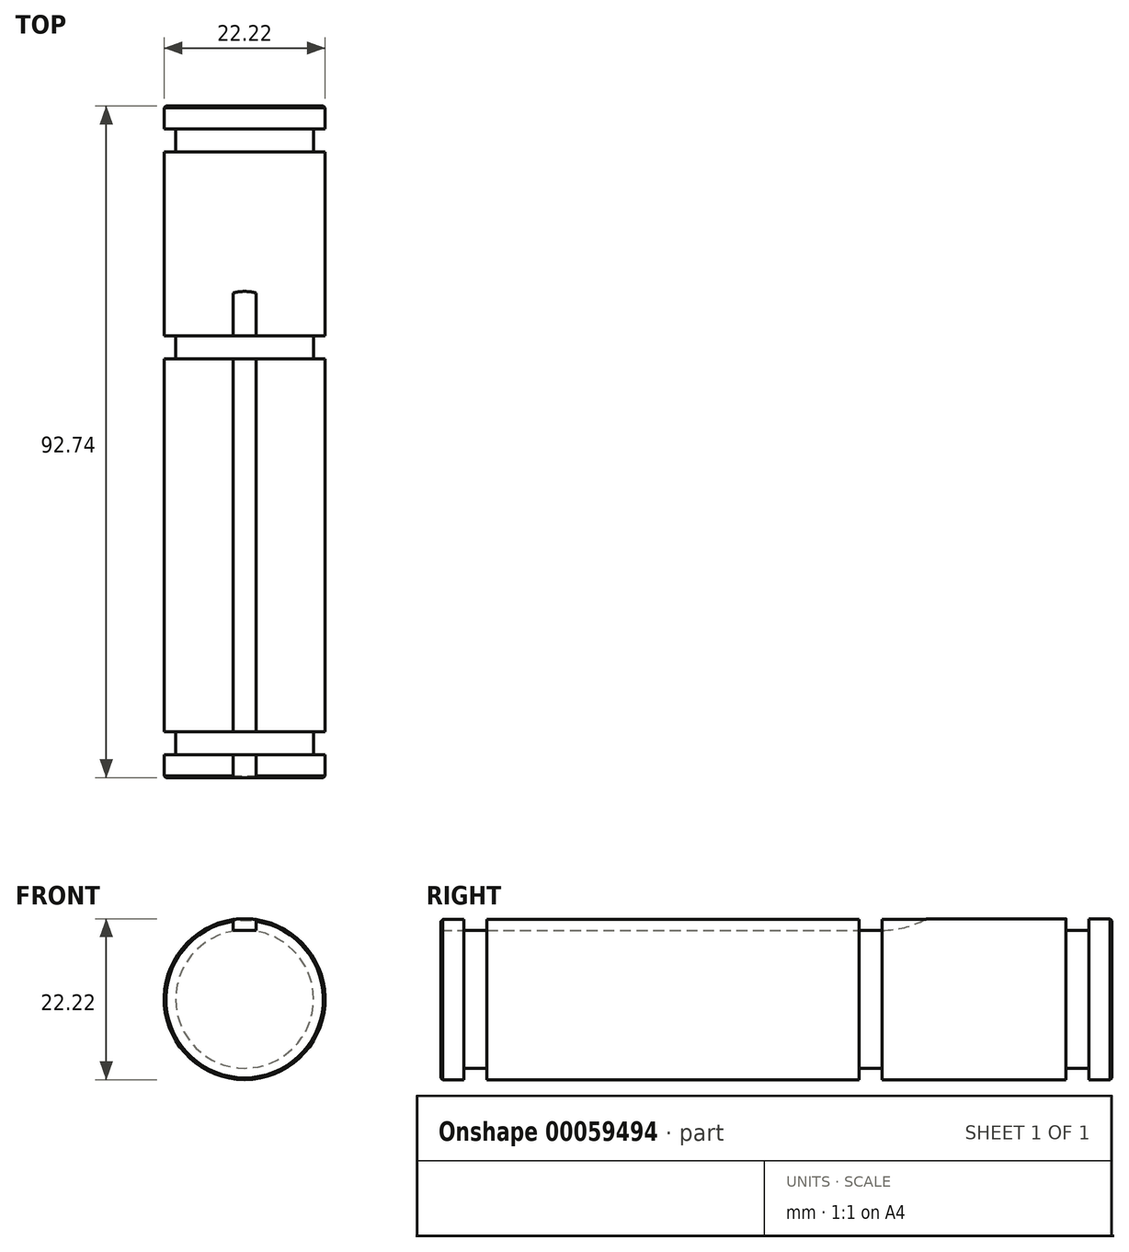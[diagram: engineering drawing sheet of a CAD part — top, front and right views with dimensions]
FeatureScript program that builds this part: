
annotation { "Feature Type Name" : "Feature", "Feature Type Description" : "" }
export const myFeature = defineFeature(function(context is Context, id is Id, definition is map)
    precondition{}
    {
        {
            var Q0;
            Q0=qCreatedBy(makeId("Front.planeOp"),FACE);
            var sketch = newSketch(context, id + "F0", { "sketchPlane" : qUnion([Q0])});
            skCircle(sketch, "E0", {"center": v(0, 0) * mm, "radius": 11.11 * mm});
            skSolve(sketch);
        }
        {
            var Q0;
            Q0=makeQuery(id+"F0.imprint","IMPRINT",FACE,{"disambiguationData":[TD([[makeQuery(id+"F0.imprint","IMPRINT",EDGE,{"derivedFrom":sQuery(id+"F0.wireOp",EDGE,"E0")}),1.0]])]});
            extrude(context, id + "F1", {"entities" : qUnion([Q0]), "oppositeDirection" : true, "depth" : 92.74 * mm});
        }
        {
            var Q0;
            Q0=qCreatedBy(makeId("Right.planeOp"),FACE);
            var sketch = newSketch(context, id + "F2", { "sketchPlane" : qUnion([Q0])});
            skLineSegment(sketch, "E1.bottom", {"start": v(0, 9.53) * mm, "end": v(60.99, 9.53) * mm});
            skLineSegment(sketch, "E1.top", {"start": v(0, 11.11) * mm, "end": v(67.13, 11.11) * mm});
            skLineSegment(sketch, "E1.left", {"start": v(0, 9.53) * mm, "end": v(0, 11.11) * mm});
            skArc(sketch, "E2.filletArc", {"start": v(60.99, 9.53) * mm, "mid": v(64.16, 9.93) * mm, "end": v(67.13, 11.11) * mm});
            skSolve(sketch);
        }
        {
            var Q0;
            Q0 = qSketchRegion(id + "F2", true);
            extrude(context, id + "F3", {"entities" : qUnion([Q0]), "operationType" : NewBodyOperationType.REMOVE, "oppositeDirection" : true, "depth" : 3.17 * mm, "symmetric" : true});
        }
        {
            var Q0;
            Q0=qCreatedBy(makeId("Right.planeOp"),FACE);
            var sketch = newSketch(context, id + "F4", { "sketchPlane" : qUnion([Q0])});
            skLineSegment(sketch, "E3.bottom", {"start": v(3.17, 9.53) * mm, "end": v(6.35, 9.53) * mm});
            skLineSegment(sketch, "E3.top", {"start": v(3.17, 11.11) * mm, "end": v(6.35, 11.11) * mm});
            skLineSegment(sketch, "E3.left", {"start": v(3.17, 9.53) * mm, "end": v(3.17, 11.11) * mm});
            skLineSegment(sketch, "E3.right", {"start": v(6.35, 9.53) * mm, "end": v(6.35, 11.11) * mm});
            skLineSegment(sketch, "E4.bottom", {"start": v(57.81, 9.53) * mm, "end": v(60.99, 9.53) * mm});
            skLineSegment(sketch, "E4.top", {"start": v(57.81, 11.11) * mm, "end": v(60.99, 11.11) * mm});
            skLineSegment(sketch, "E4.left", {"start": v(57.81, 9.53) * mm, "end": v(57.81, 11.11) * mm});
            skLineSegment(sketch, "E4.right", {"start": v(60.99, 9.53) * mm, "end": v(60.99, 11.11) * mm});
            skLineSegment(sketch, "E5.bottom", {"start": v(86.39, 9.53) * mm, "end": v(89.56, 9.53) * mm});
            skLineSegment(sketch, "E5.top", {"start": v(86.39, 11.11) * mm, "end": v(89.56, 11.11) * mm});
            skLineSegment(sketch, "E5.left", {"start": v(86.39, 9.53) * mm, "end": v(86.39, 11.11) * mm});
            skLineSegment(sketch, "E5.right", {"start": v(89.56, 9.53) * mm, "end": v(89.56, 11.11) * mm});
            skLineSegment(sketch, "E6", {"start": v(0, 0) * mm, "end": v(92.74, 0) * mm, "construction": true});
            skSolve(sketch);
        }
        {
            var Q0;
            Q0 = qSketchRegion(id + "F4", true);
            var Q1;
            Q1=sQuery(id+"F4.wireOp",EDGE,"E6");
            revolve(context, id + "F5", {"operationType" : NewBodyOperationType.REMOVE, "surfaceOperationType" : NewSurfaceOperationType.NEW, "entities" : qUnion([Q0]), "axis" : qUnion([Q1]), "revolveType" : RevolveType.FULL, "oppositeDirection" : true});
        }
        {
            var Q0;
            Q0=makeQuery(id+"F1.opExtrude","CAP_EDGE",EDGE,{"disambiguationData":[OSD([sQuery(id+"F0.wireOp",EDGE,"E0")])],"isStart":true});
            var Q1;
            Q1=makeQuery(id+"F5.boolean.opBoolean","COPY",EDGE,{"derivedFrom":makeQuery(id+"F5.opRevolve","SWEPT_EDGE",EDGE,{"disambiguationData":[OSD([sQuery(id+"F4.wireOp",EDGE,"E3.top"),sQuery(id+"F4.wireOp",EDGE,"E3.left")])]})});
            var Q2;
            Q2=makeQuery(id+"F5.boolean.opBoolean","COPY",EDGE,{"derivedFrom":makeQuery(id+"F5.opRevolve","SWEPT_EDGE",EDGE,{"disambiguationData":[OSD([sQuery(id+"F4.wireOp",EDGE,"E3.top"),sQuery(id+"F4.wireOp",EDGE,"E3.right")])]})});
            var Q3;
            Q3=makeQuery(id+"F5.boolean.opBoolean","COPY",EDGE,{"derivedFrom":makeQuery(id+"F5.opRevolve","SWEPT_EDGE",EDGE,{"disambiguationData":[OSD([sQuery(id+"F4.wireOp",EDGE,"E4.top"),sQuery(id+"F4.wireOp",EDGE,"E4.left")])]})});
            var Q4;
            Q4=makeQuery(id+"F5.boolean.opBoolean","COPY",EDGE,{"derivedFrom":makeQuery(id+"F5.opRevolve","SWEPT_EDGE",EDGE,{"disambiguationData":[OSD([sQuery(id+"F4.wireOp",EDGE,"E4.top"),sQuery(id+"F4.wireOp",EDGE,"E4.right")])]})});
            var Q5;
            Q5=makeQuery(id+"F5.boolean.opBoolean","COPY",EDGE,{"derivedFrom":makeQuery(id+"F5.opRevolve","SWEPT_EDGE",EDGE,{"disambiguationData":[OSD([sQuery(id+"F4.wireOp",EDGE,"E5.top"),sQuery(id+"F4.wireOp",EDGE,"E5.left")])]})});
            var Q6;
            Q6=makeQuery(id+"F5.boolean.opBoolean","COPY",EDGE,{"derivedFrom":makeQuery(id+"F5.opRevolve","SWEPT_EDGE",EDGE,{"disambiguationData":[OSD([sQuery(id+"F4.wireOp",EDGE,"E5.top"),sQuery(id+"F4.wireOp",EDGE,"E5.right")])]})});
            var Q7;
            Q7=makeQuery(id+"F1.opExtrude","CAP_EDGE",EDGE,{"disambiguationData":[OSD([sQuery(id+"F0.wireOp",EDGE,"E0")])],"isStart":false});
            chamfer(context, id + "F6", {"entities" : qUnion([Q0, Q1, Q2, Q3, Q4, Q5, Q6, Q7]), "width" : 0.25 * mm, "tangentPropagation" : true});
        }
    });
